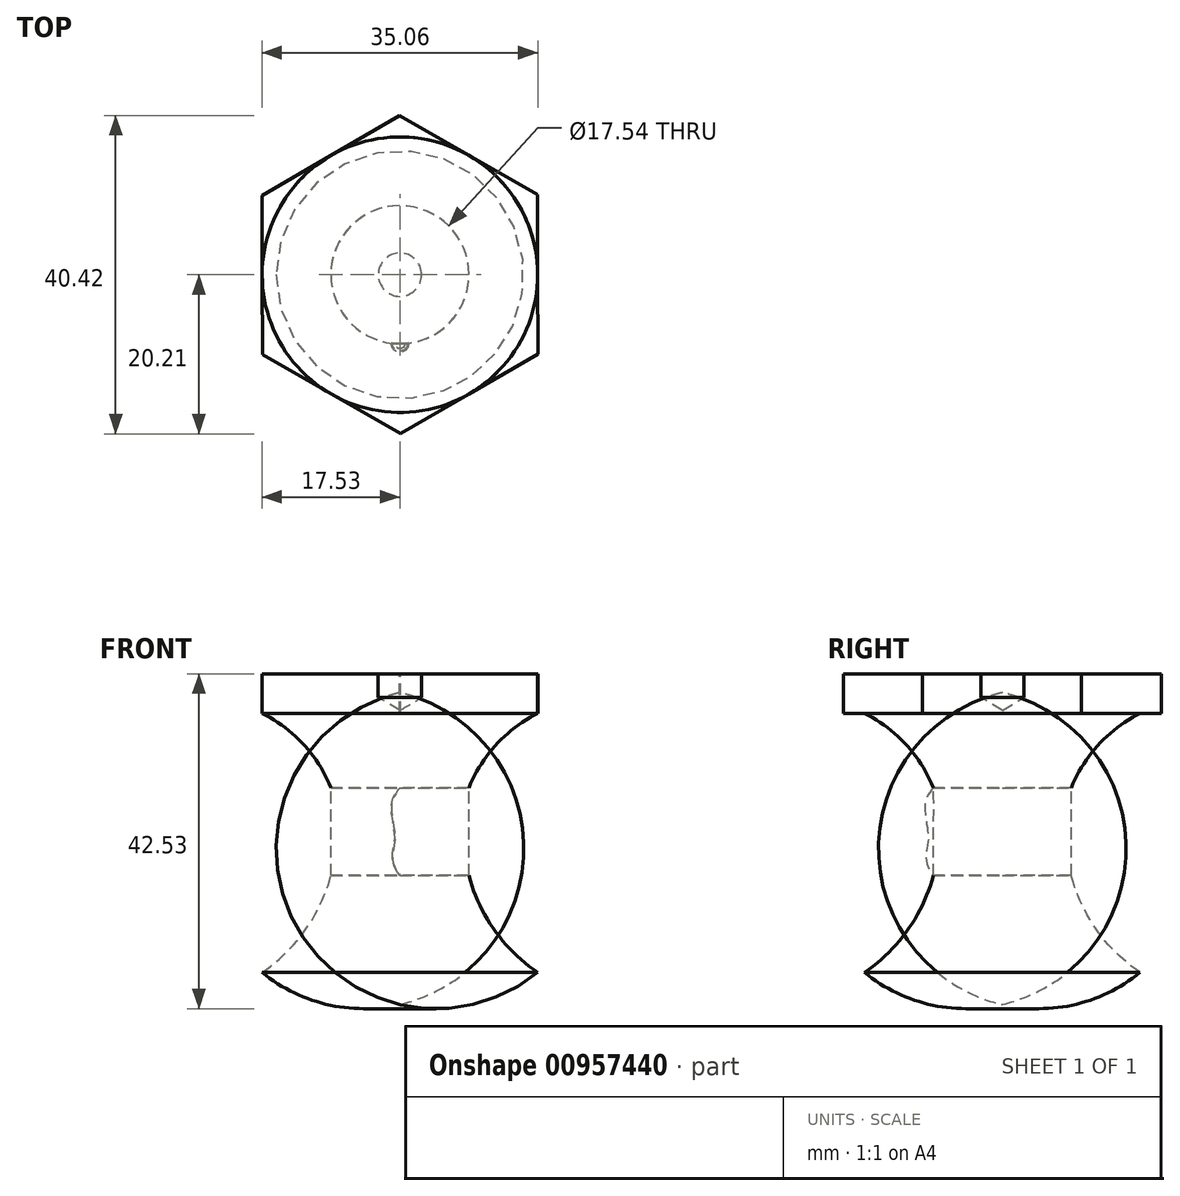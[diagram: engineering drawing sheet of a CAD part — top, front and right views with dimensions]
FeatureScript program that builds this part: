
annotation { "Feature Type Name" : "Feature", "Feature Type Description" : "" }
export const myFeature = defineFeature(function(context is Context, id is Id, definition is map)
    precondition{}
    {
        {
            var Q0;
            Q0=qCreatedBy(makeId("Top.planeOp"),FACE);
            var sketch = newSketch(context, id + "F0", { "sketchPlane" : qUnion([Q0])});
            skCircle(sketch, "E0.cCircle", {"center": v(0, 0) * mm, "radius": 17.5 * mm, "construction": true});
            skLineSegment(sketch, "E0.0", {"start": v(0.05, -20.2) * mm, "end": v(-17.47, -10.15) * mm});
            skLineSegment(sketch, "E0.1", {"start": v(-17.47, -10.15) * mm, "end": v(-17.53, 10.06) * mm});
            skLineSegment(sketch, "E0.2", {"start": v(-17.53, 10.06) * mm, "end": v(-0.05, 20.2) * mm});
            skLineSegment(sketch, "E0.3", {"start": v(-0.05, 20.2) * mm, "end": v(17.47, 10.15) * mm});
            skLineSegment(sketch, "E0.4", {"start": v(17.47, 10.15) * mm, "end": v(17.53, -10.06) * mm});
            skLineSegment(sketch, "E0.5", {"start": v(17.53, -10.06) * mm, "end": v(0.05, -20.2) * mm});
            skPoint(sketch, "E0.0.midPoint", {"position": v(-8.71, -15.18) * mm});
            skSolve(sketch);
        }
        {
            var Q0;
            Q0=makeQuery(id+"F0.imprint","IMPRINT",FACE,{"disambiguationData":[TD([[makeQuery(id+"F0.imprint","IMPRINT",EDGE,{"derivedFrom":sQuery(id+"F0.wireOp",EDGE,"E0.0")}),-1.0]])]});
            extrude(context, id + "F1", {"entities" : qUnion([Q0]), "oppositeDirection" : true, "depth" : 5 * mm, "offsetDistance" : 25 * mm});
        }
        {
            var Q0;
            Q0=qCreatedBy(makeId("Right.planeOp"),FACE);
            var sketch = newSketch(context, id + "F2", { "sketchPlane" : qUnion([Q0])});
            skArc(sketch, "E1", {"start": v(-17.5, -37.93) * mm, "mid": v(-9.22, -42) * mm, "end": v(0, -42) * mm});
            skLineSegment(sketch, "E2", {"start": v(0, -5) * mm, "end": v(-17.5, -5) * mm});
            skLineSegment(sketch, "E3", {"start": v(0, -5) * mm, "end": v(0, -42) * mm});
            skPoint(sketch, "E4.orphan", {"position": v(20.2, -5) * mm});
            skArc(sketch, "E5", {"start": v(-8.77, -14.46) * mm, "mid": v(-12.27, -8.93) * mm, "end": v(-17.5, -5) * mm});
            skArc(sketch, "E6", {"start": v(-17.5, -37.93) * mm, "mid": v(-12.03, -32.56) * mm, "end": v(-8.77, -25.63) * mm});
            skLineSegment(sketch, "E7", {"start": v(-8.77, -14.46) * mm, "end": v(-8.77, -25.63) * mm});
            skFitSpline(sketch, "E8", {"points": [v(-8.77, -25.63) * mm, v(-9.72, -23.12) * mm, v(-9.4, -20.97) * mm, v(-9.86, -16.88) * mm, v(-8.77, -14.46) * mm], "startDerivative": vector(-8.12, 9.82) * mm, "endDerivative": vector(8.42, 10.97) * mm});
            skSolve(sketch);
        }
        {
            var Q0;
            Q0=makeQuery(id+"F2.imprint","IMPRINT",FACE,{"disambiguationData":[TD([[makeQuery(id+"F2.imprint","IMPRINT",EDGE,{"derivedFrom":sQuery(id+"F2.wireOp",EDGE,"E1")}),1.0]])]});
            var Q1;
            Q1=sQuery(id+"F2.wireOp",EDGE,"E3");
            revolve(context, id + "F3", {"operationType" : NewBodyOperationType.ADD, "surfaceOperationType" : NewSurfaceOperationType.NEW, "entities" : qUnion([Q0]), "axis" : qUnion([Q1]), "revolveType" : RevolveType.FULL});
        }
        {
            var Q0;
            Q0=sQuery(id+"F0.wireOp",VERTEX,"E0.cCircle.center");
            var Q1;
            Q1=makeQuery(id+"F1.opExtrude","SWEPT_BODY",BODY,{"disambiguationData":[OSD([sQuery(id+"F0.wireOp",EDGE,"E0.0"),sQuery(id+"F0.wireOp",EDGE,"E0.1"),sQuery(id+"F0.wireOp",EDGE,"E0.2"),sQuery(id+"F0.wireOp",EDGE,"E0.3"),sQuery(id+"F0.wireOp",EDGE,"E0.4"),sQuery(id+"F0.wireOp",EDGE,"E0.5")])]});
            hole(context, id + "F4", {"style" : HoleStyle.SIMPLE, "endStyle" : HoleEndStyle.BLIND, "holeDiameter" : 5.5 * mm, "majorDiameter" : 5 * mm, "holeDepth" : 3 * mm, "isTappedThrough" : true, "tappedDepth" : 12 * mm, "tapClearance" : 3, "locations" : qUnion([Q0]), "scope" : qUnion([Q1])});
        }
        {
            var Q0;
            Q0=makeQuery(id+"F2.imprint","IMPRINT",FACE,{"disambiguationData":[TD([[makeQuery(id+"F2.imprint","IMPRINT",EDGE,{"derivedFrom":sQuery(id+"F2.wireOp",EDGE,"E7")}),-1.0]])]});
            var Q1;
            Q1=sQuery(id+"F2.wireOp",EDGE,"E7");
            revolve(context, id + "F5", {"operationType" : NewBodyOperationType.ADD, "surfaceOperationType" : NewSurfaceOperationType.NEW, "entities" : qUnion([Q0]), "axis" : qUnion([Q1]), "revolveType" : RevolveType.FULL});
        }
    });
